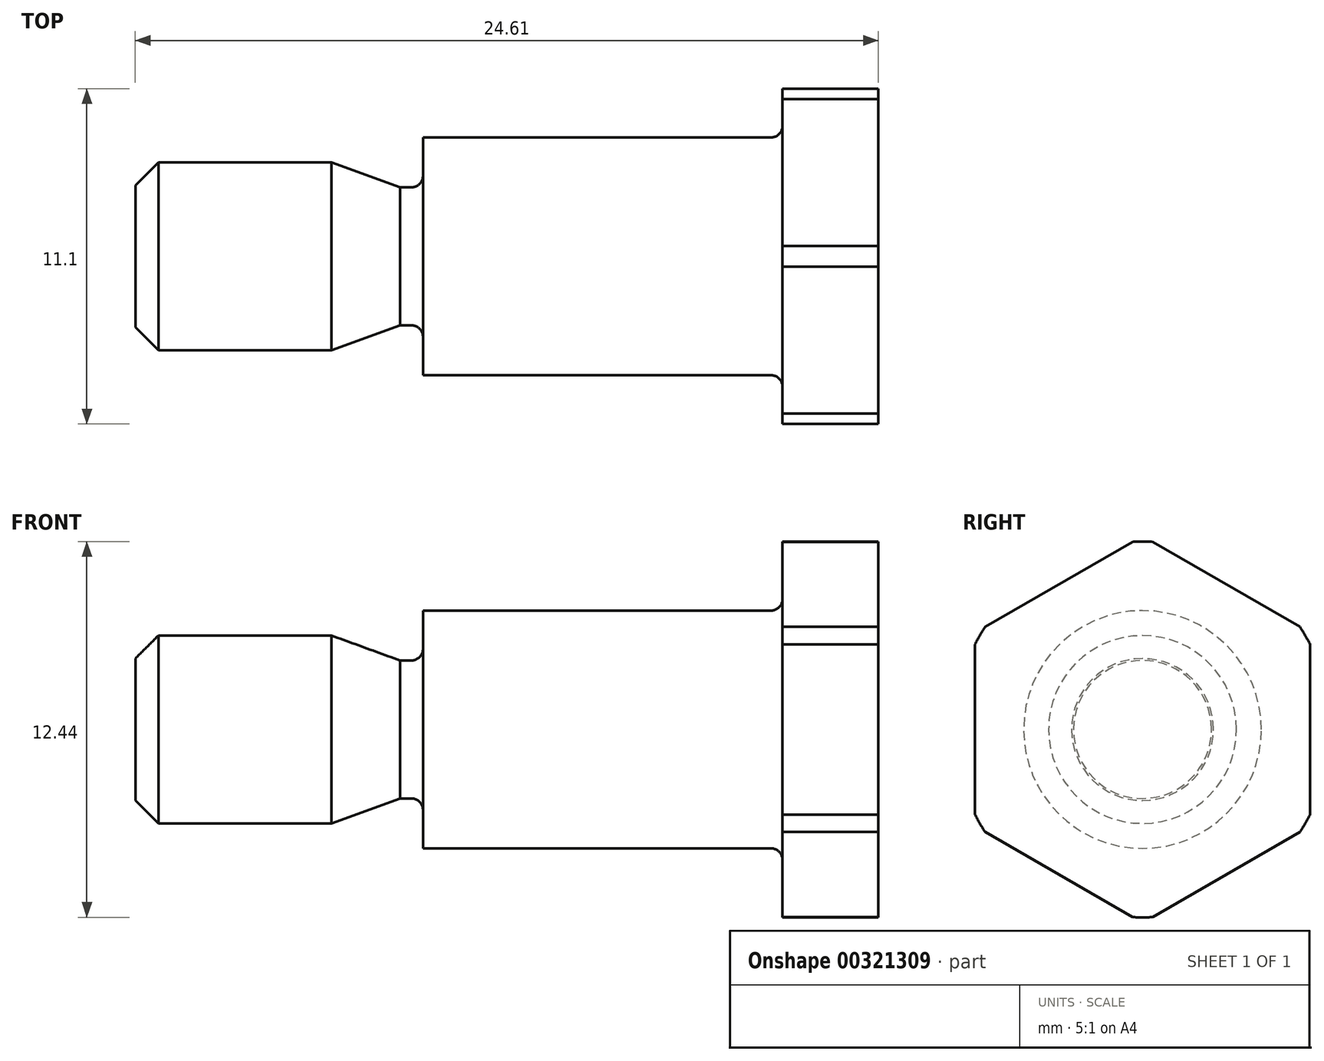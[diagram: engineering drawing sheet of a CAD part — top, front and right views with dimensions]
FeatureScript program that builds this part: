
annotation { "Feature Type Name" : "Feature", "Feature Type Description" : "" }
export const myFeature = defineFeature(function(context is Context, id is Id, definition is map)
    precondition{}
    {
        {
            var Q0;
            Q0=qCreatedBy(makeId("Front.planeOp"),FACE);
            var sketch = newSketch(context, id + "F0", { "sketchPlane" : qUnion([Q0])});
            skLineSegment(sketch, "E0", {"start": v(0, 0) * mm, "end": v(-24.6, 0) * mm});
            skLineSegment(sketch, "E1", {"start": v(-24.6, 0) * mm, "end": v(-24.6, 3.11) * mm});
            skLineSegment(sketch, "E2", {"start": v(-24.6, 3.11) * mm, "end": v(-18.11, 3.11) * mm});
            skLineSegment(sketch, "E3", {"start": v(-15.08, 2.29) * mm, "end": v(-15.08, 3.94) * mm});
            skLineSegment(sketch, "E4", {"start": v(-15.08, 3.94) * mm, "end": v(-3.17, 3.94) * mm});
            skLineSegment(sketch, "E5", {"start": v(-3.18, 3.94) * mm, "end": v(-3.18, 6.22) * mm});
            skLineSegment(sketch, "E6", {"start": v(-3.18, 6.22) * mm, "end": v(0, 6.22) * mm});
            skLineSegment(sketch, "E7", {"start": v(0, 6.22) * mm, "end": v(0, 0) * mm});
            skLineSegment(sketch, "E8", {"start": v(0, 0) * mm, "end": v(5.6, 0) * mm, "construction": true});
            skLineSegment(sketch, "E9", {"start": v(-18.11, 3.11) * mm, "end": v(-15.84, 2.29) * mm});
            skLineSegment(sketch, "E10", {"start": v(-15.84, 2.29) * mm, "end": v(-15.08, 2.29) * mm});
            skSolve(sketch);
        }
        {
            var Q0;
            Q0 = qSketchRegion(id + "F0", true);
            var Q1;
            Q1=sQuery(id+"F0.wireOp",EDGE,"E8");
            revolve(context, id + "F1", {"surfaceOperationType" : NewSurfaceOperationType.NEW, "entities" : qUnion([Q0]), "axis" : qUnion([Q1]), "revolveType" : RevolveType.FULL});
        }
        {
            var Q0;
            Q0=makeQuery(id+"F1.opRevolve","SWEPT_FACE",FACE,{"disambiguationData":[OSD([sQuery(id+"F0.wireOp",EDGE,"E7")])]});
            var sketch = newSketch(context, id + "F2", { "sketchPlane" : qUnion([Q0])});
            skCircle(sketch, "E11.cCircle", {"center": v(0, 0) * mm, "radius": 6.4 * mm, "construction": true});
            skLineSegment(sketch, "E11.0", {"start": v(0, 6.4) * mm, "end": v(5.55, 3.2) * mm});
            skLineSegment(sketch, "E11.1", {"start": v(5.55, 3.2) * mm, "end": v(5.55, -3.2) * mm});
            skLineSegment(sketch, "E11.2", {"start": v(5.55, -3.2) * mm, "end": v(0, -6.4) * mm});
            skLineSegment(sketch, "E11.3", {"start": v(0, -6.4) * mm, "end": v(-5.55, -3.2) * mm});
            skLineSegment(sketch, "E11.4", {"start": v(-5.55, -3.2) * mm, "end": v(-5.55, 3.2) * mm});
            skLineSegment(sketch, "E11.5", {"start": v(-5.55, 3.2) * mm, "end": v(0, 6.4) * mm});
            skSolve(sketch);
        }
        {
            var Q0;
            {var subQ0=sQuery(id+"F2.wireOp",EDGE,"E11.5");Q0=makeQuery(id+"F2.imprint","IMPRINT",FACE,{"disambiguationData":[TD([[makeQuery(id+"F2.imprint","IMPRINT",EDGE,{"derivedFrom":subQ0}),1.0]])]});}
            var Q1;
            {var subQ0=sQuery(id+"F2.wireOp",EDGE,"E11.0");Q1=makeQuery(id+"F2.imprint","IMPRINT",FACE,{"disambiguationData":[TD([[makeQuery(id+"F2.imprint","IMPRINT",EDGE,{"derivedFrom":subQ0}),1.0]])]});}
            var Q2;
            {var subQ0=sQuery(id+"F2.wireOp",EDGE,"E11.1");Q2=makeQuery(id+"F2.imprint","IMPRINT",FACE,{"disambiguationData":[TD([[makeQuery(id+"F2.imprint","IMPRINT",EDGE,{"derivedFrom":subQ0}),1.0]])]});}
            var Q3;
            {var subQ0=sQuery(id+"F2.wireOp",EDGE,"E11.2");Q3=makeQuery(id+"F2.imprint","IMPRINT",FACE,{"disambiguationData":[TD([[makeQuery(id+"F2.imprint","IMPRINT",EDGE,{"derivedFrom":subQ0}),1.0]])]});}
            var Q4;
            {var subQ0=sQuery(id+"F2.wireOp",EDGE,"E11.3");Q4=makeQuery(id+"F2.imprint","IMPRINT",FACE,{"disambiguationData":[TD([[makeQuery(id+"F2.imprint","IMPRINT",EDGE,{"derivedFrom":subQ0}),1.0]])]});}
            var Q5;
            {var subQ0=sQuery(id+"F2.wireOp",EDGE,"E11.4");Q5=makeQuery(id+"F2.imprint","IMPRINT",FACE,{"disambiguationData":[TD([[makeQuery(id+"F2.imprint","IMPRINT",EDGE,{"derivedFrom":subQ0}),1.0]])]});}
            extrude(context, id + "F3", {"entities" : qUnion([Q0, Q1, Q2, Q3, Q4, Q5]), "operationType" : NewBodyOperationType.REMOVE, "endBound" : BoundingType.UP_TO_NEXT, "oppositeDirection" : true, "depth" : 25.4 * mm, "offsetDistance" : 25.4 * mm});
        }
        {
            var Q0;
            Q0=makeQuery(id+"F1.opRevolve","SWEPT_EDGE",EDGE,{"disambiguationData":[OSD([sQuery(id+"F0.wireOp",EDGE,"E1"),sQuery(id+"F0.wireOp",EDGE,"E2")])]});
            chamfer(context, id + "F4", {"entities" : qUnion([Q0]), "width" : 0.76 * mm, "tangentPropagation" : true});
        }
        {
            var Q0;
            Q0=makeQuery(id+"F1.opRevolve","SWEPT_EDGE",EDGE,{"disambiguationData":[OSD([sQuery(id+"F0.wireOp",EDGE,"E4"),sQuery(id+"F0.wireOp",EDGE,"E5")])]});
            fillet(context, id + "F5", {"entities" : qUnion([Q0]), "radius" : 0.38 * mm, "tangentPropagation" : true, "allowEdgeOverflow" : false});
        }
        {
            var Q0;
            Q0=makeQuery(id+"F1.opRevolve","SWEPT_EDGE",EDGE,{"disambiguationData":[OSD([sQuery(id+"F0.wireOp",EDGE,"E3"),sQuery(id+"F0.wireOp",EDGE,"E10")])]});
            fillet(context, id + "F6", {"entities" : qUnion([Q0]), "radius" : 0.38 * mm, "tangentPropagation" : true, "allowEdgeOverflow" : false});
        }
    });
